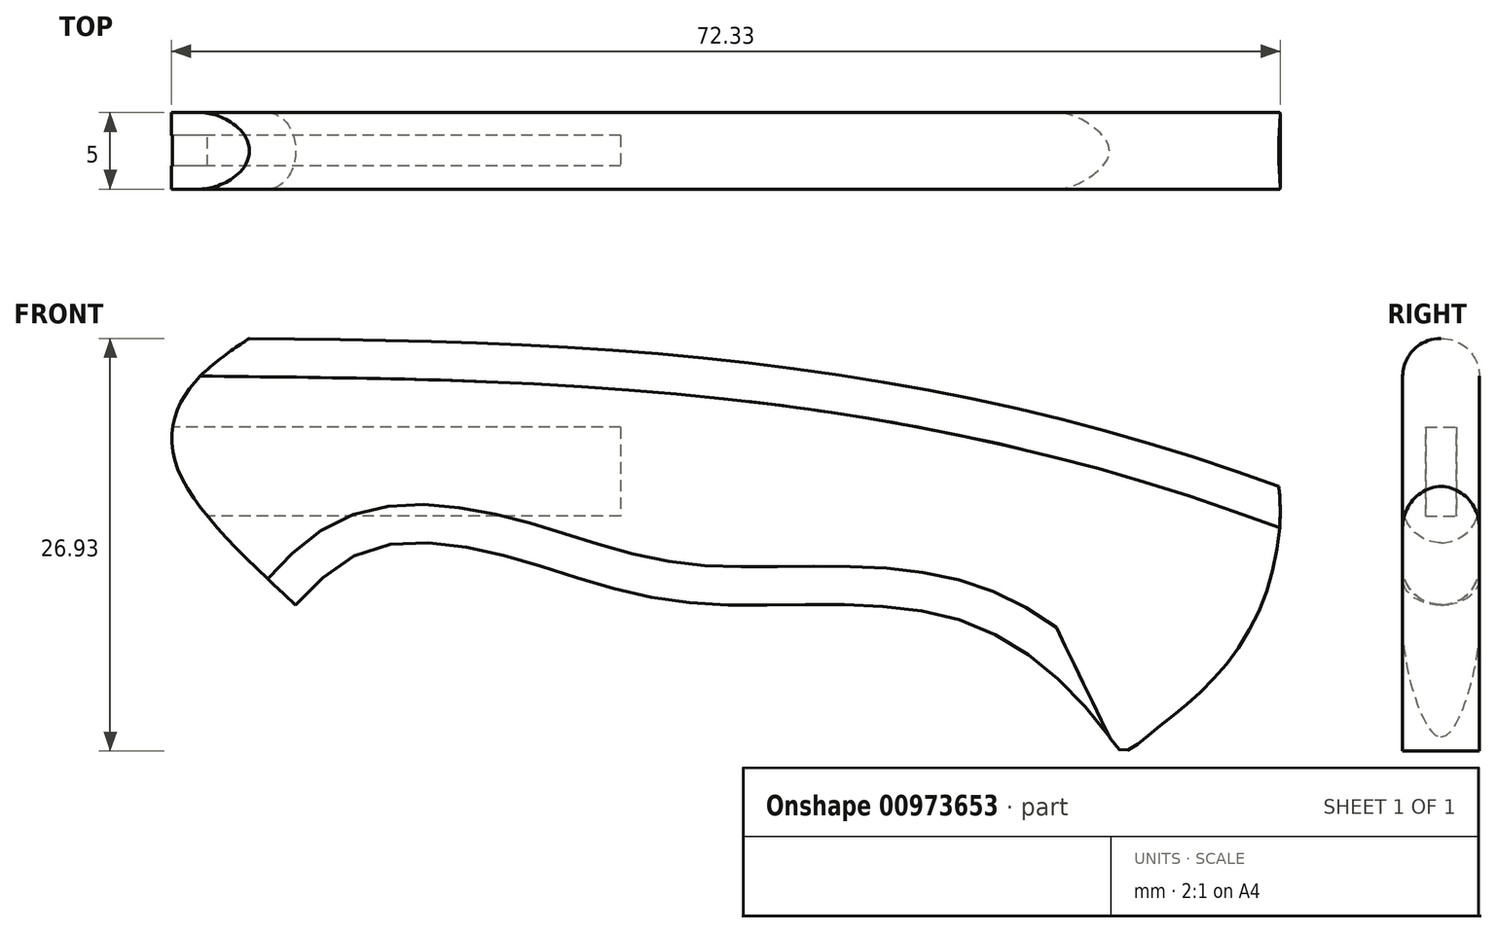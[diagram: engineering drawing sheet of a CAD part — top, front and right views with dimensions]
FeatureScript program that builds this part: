
annotation { "Feature Type Name" : "Feature", "Feature Type Description" : "" }
export const myFeature = defineFeature(function(context is Context, id is Id, definition is map)
    precondition{}
    {
        {
            var Q0;
            Q0=qCreatedBy(makeId("Front.planeOp"),FACE);
            var sketch = newSketch(context, id + "F0", { "sketchPlane" : qUnion([Q0])});
            skFitSpline(sketch, "E0", {"points": [v(30.37, 22) * mm, v(60.1, 20.7) * mm, v(97.54, 12.32) * mm], "startDerivative": vector(61.31, -0.7) * mm, "endDerivative": vector(73.58, -27.18) * mm});
            skFitSpline(sketch, "E1", {"points": [v(97.54, 12.32) * mm, v(94.6, 1.32) * mm, v(88.72, -4.17) * mm, v(86.5, -4.03) * mm], "startDerivative": vector(3.1, -27.05) * mm, "endDerivative": vector(-11.16, 23) * mm});
            skFitSpline(sketch, "E2", {"points": [v(86.5, -4.03) * mm, v(75, 4.06) * mm, v(58.77, 4.76) * mm, v(48.08, 7.52) * mm, v(39.62, 8.54) * mm, v(33.39, 4.58) * mm], "startDerivative": vector(-45.31, 60.31) * mm, "endDerivative": vector(-41.35, -46.8) * mm});
            skFitSpline(sketch, "E3", {"points": [v(33.39, 4.58) * mm, v(25.52, 13.96) * mm, v(26.43, 18.67) * mm, v(30.37, 22) * mm], "startDerivative": vector(-23.9, 22.26) * mm, "endDerivative": vector(15.52, 10.43) * mm});
            skSolve(sketch);
        }
        {
            var Q0;
            Q0=makeQuery(id+"F0.imprint","IMPRINT",FACE,{"disambiguationData":[TD([[makeQuery(id+"F0.imprint","IMPRINT",EDGE,{"derivedFrom":sQuery(id+"F0.wireOp",EDGE,"E0")}),-1.0]])]});
            extrude(context, id + "F1", {"entities" : qUnion([Q0]), "depth" : 5 * mm, "offsetDistance" : 25 * mm});
        }
        {
            var Q0;
            Q0=makeQuery(id+"F1.opExtrude","CAP_EDGE",EDGE,{"disambiguationData":[OSD([sQuery(id+"F0.wireOp",EDGE,"E0")])],"isStart":false});
            var Q1;
            Q1=makeQuery(id+"F1.opExtrude","CAP_EDGE",EDGE,{"disambiguationData":[OSD([sQuery(id+"F0.wireOp",EDGE,"E0")])],"isStart":true});
            fillet(context, id + "F2", {"entities" : qUnion([Q0, Q1]), "radius" : 2.5 * mm, "tangentPropagation" : true, "allowEdgeOverflow" : false});
        }
        {
            var Q0;
            Q0=makeQuery(id+"F1.opExtrude","CAP_EDGE",EDGE,{"disambiguationData":[OSD([sQuery(id+"F0.wireOp",EDGE,"E2")])],"isStart":false});
            var Q1;
            Q1=makeQuery(id+"F1.opExtrude","CAP_EDGE",EDGE,{"disambiguationData":[OSD([sQuery(id+"F0.wireOp",EDGE,"E2")])],"isStart":true});
            fillet(context, id + "F3", {"entities" : qUnion([Q0, Q1]), "radius" : 2.5 * mm, "tangentPropagation" : true, "allowEdgeOverflow" : false});
        }
        {
            var Q0;
            Q0=qCreatedBy(makeId("Right.planeOp"),FACE);
            var sketch = newSketch(context, id + "F4", { "sketchPlane" : qUnion([Q0])});
            skLineSegment(sketch, "E4.bottom", {"start": v(-1.5, 16.2) * mm, "end": v(-3.5, 16.2) * mm});
            skLineSegment(sketch, "E4.top", {"start": v(-1.5, 10.38) * mm, "end": v(-3.5, 10.38) * mm});
            skLineSegment(sketch, "E4.left", {"start": v(-1.5, 16.2) * mm, "end": v(-1.5, 10.38) * mm});
            skLineSegment(sketch, "E4.right", {"start": v(-3.5, 16.2) * mm, "end": v(-3.5, 10.38) * mm});
            skPoint(sketch, "E4.middle", {"position": v(-2.5, 13.3) * mm});
            skSolve(sketch);
        }
        {
            var Q0;
            Q0=makeQuery(id+"F4.imprint","IMPRINT",FACE,{"disambiguationData":[TD([[makeQuery(id+"F4.imprint","IMPRINT",EDGE,{"derivedFrom":sQuery(id+"F4.wireOp",EDGE,"E4.bottom")}),1.0]])]});
            extrude(context, id + "F5", {"entities" : qUnion([Q0]), "operationType" : NewBodyOperationType.REMOVE, "depth" : 54.6 * mm, "offsetDistance" : 25 * mm});
        }
    });
